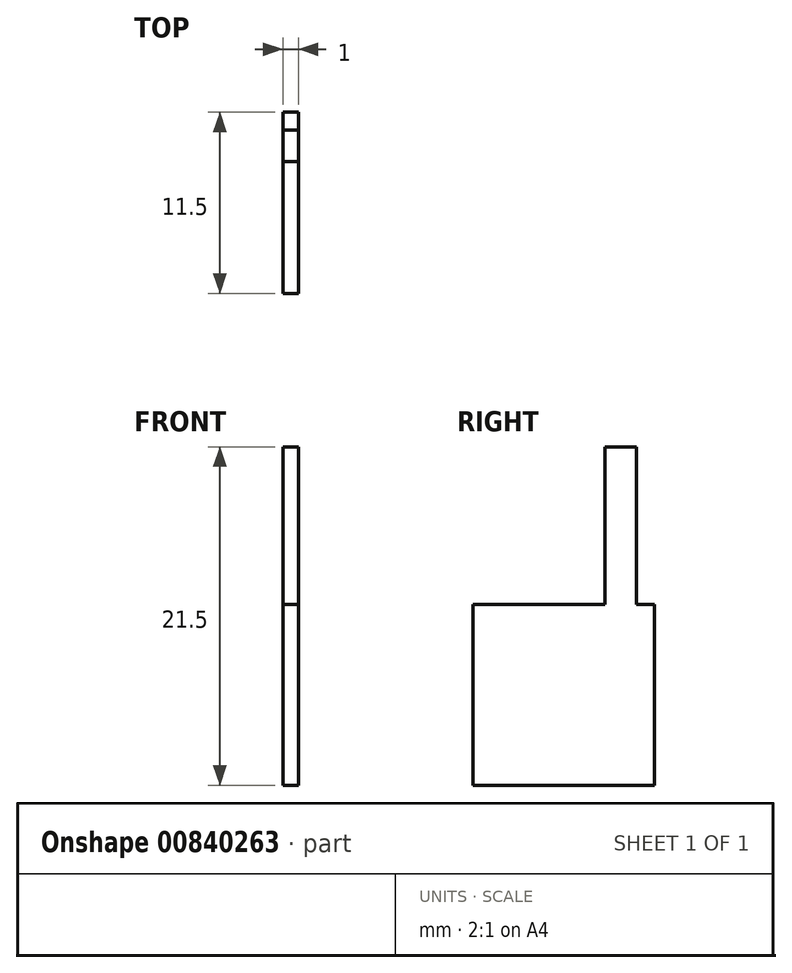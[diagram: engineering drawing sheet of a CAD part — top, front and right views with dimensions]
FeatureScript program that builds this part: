
annotation { "Feature Type Name" : "Feature", "Feature Type Description" : "" }
export const myFeature = defineFeature(function(context is Context, id is Id, definition is map)
    precondition{}
    {
        {
            var Q0;
            Q0=qCreatedBy(makeId("Right.planeOp"),FACE);
            var sketch = newSketch(context, id + "F0", { "sketchPlane" : qUnion([Q0])});
            skLineSegment(sketch, "E0.bottom", {"start": v(0, 0) * mm, "end": v(8.38, 0) * mm});
            skLineSegment(sketch, "E0.top", {"start": v(0, -11.5) * mm, "end": v(11.5, -11.5) * mm});
            skLineSegment(sketch, "E0.left", {"start": v(0, 0) * mm, "end": v(0, -11.5) * mm});
            skLineSegment(sketch, "E1", {"start": v(11.5, 0) * mm, "end": v(11.5, -11.5) * mm});
            skLineSegment(sketch, "E2", {"start": v(10.38, 0) * mm, "end": v(10.38, 10) * mm});
            skLineSegment(sketch, "E3", {"start": v(10.38, 10) * mm, "end": v(8.38, 10) * mm});
            skLineSegment(sketch, "E4", {"start": v(8.38, 10) * mm, "end": v(8.38, 0) * mm});
            skLineSegment(sketch, "E5.trimOffspring", {"start": v(10.38, 0) * mm, "end": v(11.5, 0) * mm});
            skSolve(sketch);
        }
        {
            var Q0;
            Q0=makeQuery(id+"F0.imprint","IMPRINT",FACE,{"disambiguationData":[TD([[makeQuery(id+"F0.imprint","IMPRINT",EDGE,{"derivedFrom":sQuery(id+"F0.wireOp",EDGE,"E0.bottom")}),-1.0]])]});
            var Q1;
            Q1=makeQuery(id+"F0.imprint","IMPRINT",FACE,{"disambiguationData":[TD([[makeQuery(id+"F0.imprint","IMPRINT",EDGE,{"derivedFrom":sQuery(id+"F0.wireOp",EDGE,"r65wuaeR-pUGk-UfhY-v5oq-7bkjaNJfQmKm.bottom")}),-1.0]])]});
            var Q2;
            Q2=makeQuery(id+"F0.imprint","IMPRINT",FACE,{"disambiguationData":[TD([[makeQuery(id+"F0.imprint","IMPRINT",EDGE,{"derivedFrom":sQuery(id+"F0.wireOp",EDGE,"n5EaUuf3-CoM6-EQkv-XzT1-ydr3onYee1LO.bottom")}),1.0]])]});
            var Q3;
            Q3=makeQuery(id+"F0.imprint","IMPRINT",FACE,{"disambiguationData":[TD([[makeQuery(id+"F0.imprint","IMPRINT",EDGE,{"derivedFrom":sQuery(id+"F0.wireOp",EDGE,"2NUbogVr-x7fL-9LVX-WR3f-6RiyyzUn8nbi.bottom")}),-1.0]])]});
            extrude(context, id + "F1", {"entities" : qUnion([Q0, Q1, Q2, Q3]), "depth" : 1 * mm, "offsetDistance" : 25 * mm});
        }
    });
